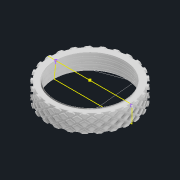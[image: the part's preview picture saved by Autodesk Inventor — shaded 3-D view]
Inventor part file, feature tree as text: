
AUTODESK INVENTOR PART (.ipt)
format: ipt  version: 2021.3 (Build 253353000, 353)  size: 1,614,336 bytes
history: native  units: mm
features: helix x6, sketch x4, pattern_circular x2, extrude x1, draft x1
ambient origin geometry x8: Origin, YZ Plane, XZ Plane, XY Plane, X Axis, Y Axis, Z Axis, Center Point
bodies: Solid1 (feature_tree)
feature tree (14):
  extrude  "Extrusion1"  Depth=6.52mm TaperAngle=0.0deg
  draft  "FaceDraft1"
  sketch  "Sketch2"  dims[d7=2.0mm d8=9.0mm d9=10.0mm d10=1.047198mm d11=90.0deg d12=90.0deg d13=0.0mm d14=0.0mm d15=2.0mm d16=3.0mm d17=10.0mm d18=-1.047198mm d19=90.0deg d20=90.0deg d21=0.0mm d22=0.0mm d23=3.0mm]
  sketch  "Sketch4"  dims[d52=70.0mm d53=9.0mm d54=10.0mm d55=0.0mm d56=90.0deg d57=90.0deg d58=0.0mm d59=0.0mm d60=70.0mm d61=9.0mm d62=10.0mm d63=0.0mm d64=90.0deg d65=90.0deg d66=0.0mm d67=0.0mm d68=250.0mm d69=360.0deg]
  helix  "Coil1"  [1 undecoded]
  helix  "Coil2"  [1 undecoded]
  sketch  "Sketch7"  dims[d71=70.0mm d72=9.0mm d73=10.0mm d74=0.0mm d75=90.0deg d76=90.0deg d77=0.0mm d78=0.0mm d79=70.0mm d80=9.0mm d81=10.0mm d82=0.0mm d83=90.0deg d84=90.0deg d85=0.0mm d86=0.0mm d87=250.0mm d88=360.0deg]
  helix  "Coil6"  [1 undecoded]
  helix  "Coil7"  [1 undecoded]
  pattern_circular  "Circular Pattern1"  [2 undecoded]
  helix  "Coil8"  [1 undecoded]
  helix  "Coil9"  [1 undecoded]
  pattern_circular  "Circular Pattern2"  [2 undecoded]
  sketch  "Sketch1"  dims[d0=26.5mm d2=6.52mm d3=0.0mm d4=1.047198mm]
note: 10 required parameter values undecoded (feature->parameter linkage not recoverable at this tier; creation-order binding heuristic only, values carry confidence <= 0.55)
